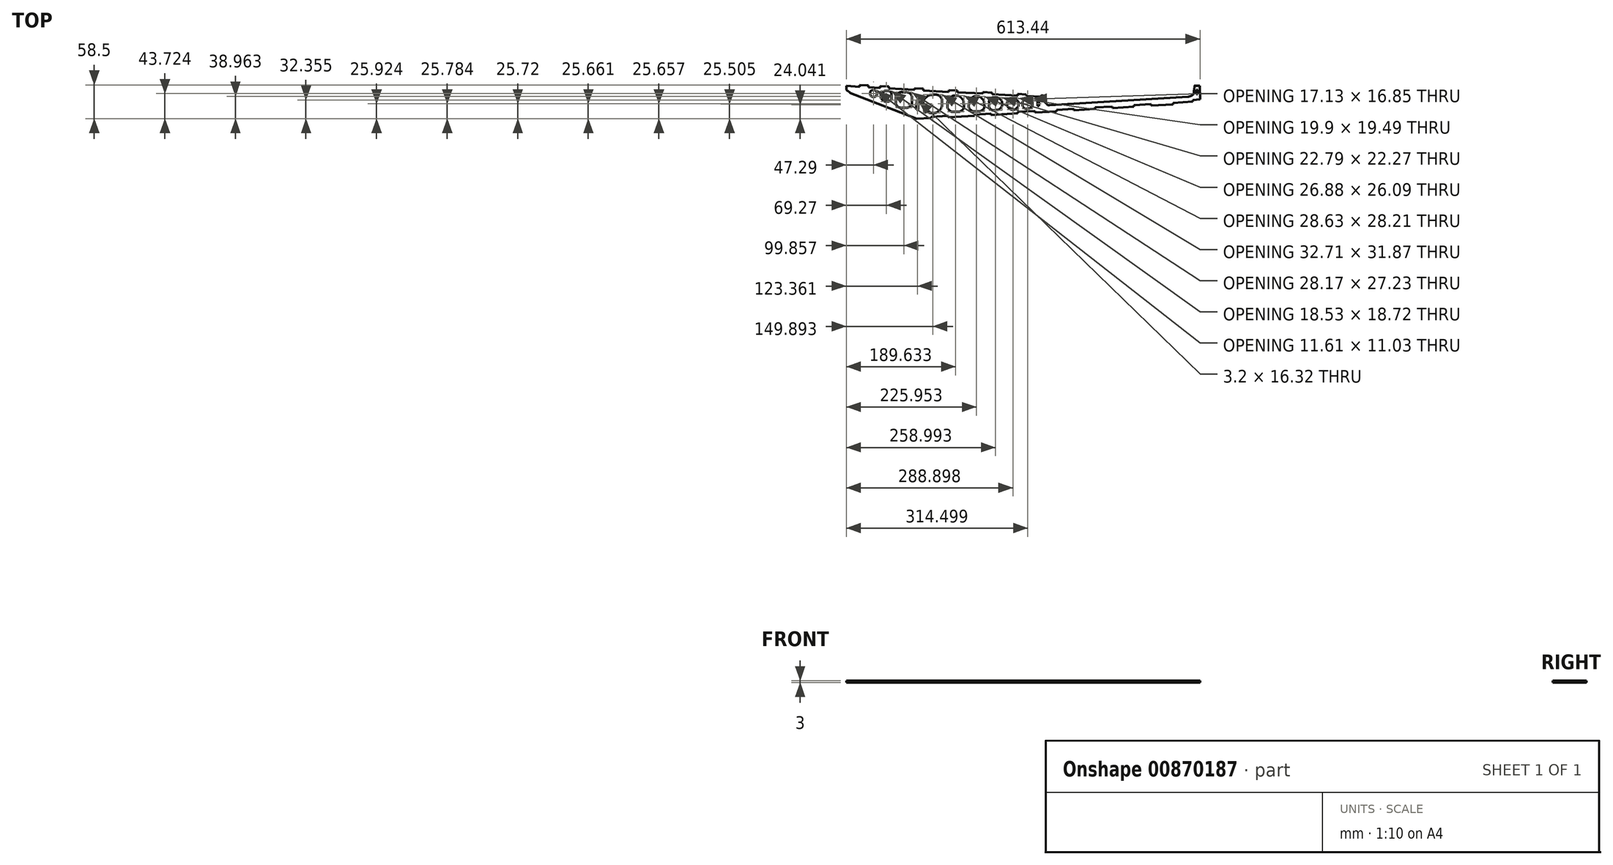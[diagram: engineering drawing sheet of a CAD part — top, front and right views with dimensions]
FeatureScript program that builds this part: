
annotation { "Feature Type Name" : "Feature", "Feature Type Description" : "" }
export const myFeature = defineFeature(function(context is Context, id is Id, definition is map)
    precondition{}
    {
        {
            var Q0;
            Q0=qCreatedBy(makeId("Top.planeOp"),FACE);
            var sketch = newSketch(context, id + "F0", { "sketchPlane" : qUnion([Q0])});
            skLineSegment(sketch, "E0", {"start": v(-306.53, 27.6) * mm, "end": v(-283.7, 26.24) * mm});
            skLineSegment(sketch, "E1", {"start": v(-283.7, 26.24) * mm, "end": v(-283.65, 29.25) * mm});
            skLineSegment(sketch, "E2", {"start": v(-283.65, 29.25) * mm, "end": v(-268.49, 28.33) * mm});
            skLineSegment(sketch, "E3", {"start": v(-268.49, 28.33) * mm, "end": v(-268.62, 25.37) * mm});
            skLineSegment(sketch, "E4", {"start": v(-268.62, 25.37) * mm, "end": v(-248.2, 24.14) * mm});
            skLineSegment(sketch, "E5", {"start": v(-248.2, 24.14) * mm, "end": v(-248.23, 27.11) * mm});
            skLineSegment(sketch, "E6", {"start": v(-248.23, 27.11) * mm, "end": v(-233.12, 26.42) * mm});
            skLineSegment(sketch, "E7", {"start": v(-233.12, 26.42) * mm, "end": v(-233.28, 23.32) * mm});
            skLineSegment(sketch, "E8", {"start": v(-233.28, 23.32) * mm, "end": v(-188.42, 20.66) * mm});
            skLineSegment(sketch, "E9", {"start": v(-188.42, 20.66) * mm, "end": v(-188.4, 23.56) * mm});
            skLineSegment(sketch, "E10", {"start": v(-188.4, 23.56) * mm, "end": v(-173.4, 22.68) * mm});
            skLineSegment(sketch, "E11", {"start": v(-173.4, 22.68) * mm, "end": v(-173.39, 19.88) * mm});
            skLineSegment(sketch, "E12", {"start": v(-173.39, 19.88) * mm, "end": v(-129.24, 17.14) * mm});
            skLineSegment(sketch, "E13", {"start": v(-129.24, 17.14) * mm, "end": v(-129.1, 20.23) * mm});
            skLineSegment(sketch, "E14", {"start": v(-129.1, 20.23) * mm, "end": v(-114.05, 19.46) * mm});
            skLineSegment(sketch, "E15", {"start": v(-114.05, 19.46) * mm, "end": v(-114.17, 16.65) * mm});
            skLineSegment(sketch, "E16", {"start": v(-114.17, 16.65) * mm, "end": v(-69.6, 14.2) * mm});
            skLineSegment(sketch, "E17", {"start": v(-69.6, 14.2) * mm, "end": v(-69.49, 16.95) * mm});
            skLineSegment(sketch, "E18", {"start": v(-69.49, 16.95) * mm, "end": v(-54.08, 15.88) * mm});
            skLineSegment(sketch, "E19", {"start": v(-54.08, 15.88) * mm, "end": v(-53.85, 13.26) * mm});
            skLineSegment(sketch, "E20", {"start": v(-53.85, 13.26) * mm, "end": v(-9.62, 10.9) * mm});
            skLineSegment(sketch, "E21", {"start": v(-9.62, 10.9) * mm, "end": v(-9.38, 14.01) * mm});
            skLineSegment(sketch, "E22", {"start": v(-9.38, 14.01) * mm, "end": v(5.44, 12.76) * mm});
            skLineSegment(sketch, "E23", {"start": v(5.44, 12.76) * mm, "end": v(5.67, 9.87) * mm});
            skLineSegment(sketch, "E24", {"start": v(5.67, 9.87) * mm, "end": v(31.56, 8.9) * mm});
            skLineSegment(sketch, "E25", {"start": v(31.56, 8.9) * mm, "end": v(31.93, 11.73) * mm});
            skLineSegment(sketch, "E26", {"start": v(45.61, -5.69) * mm, "end": v(285.73, 8.77) * mm});
            skLineSegment(sketch, "E27", {"start": v(296.22, 19.12) * mm, "end": v(297, 26.85) * mm});
            skLineSegment(sketch, "E28", {"start": v(298.34, 28) * mm, "end": v(306.34, 28.12) * mm});
            skLineSegment(sketch, "E29", {"start": v(306.34, 28.12) * mm, "end": v(306.53, 4.6) * mm});
            skLineSegment(sketch, "E30", {"start": v(306.53, 4.6) * mm, "end": v(294.22, 3.28) * mm});
            skLineSegment(sketch, "E31", {"start": v(294.22, 3.28) * mm, "end": v(294.32, 0.27) * mm});
            skLineSegment(sketch, "E32", {"start": v(294.32, 0.27) * mm, "end": v(259.45, -1.91) * mm});
            skLineSegment(sketch, "E33", {"start": v(259.45, -1.91) * mm, "end": v(259.47, -4.56) * mm});
            skLineSegment(sketch, "E34", {"start": v(259.47, -4.56) * mm, "end": v(221.44, -6.56) * mm});
            skLineSegment(sketch, "E35", {"start": v(221.44, -6.56) * mm, "end": v(221.44, -4.07) * mm});
            skLineSegment(sketch, "E36", {"start": v(221.44, -4.07) * mm, "end": v(191.93, -5.9) * mm});
            skLineSegment(sketch, "E37", {"start": v(191.93, -5.9) * mm, "end": v(191.94, -8.45) * mm});
            skLineSegment(sketch, "E38", {"start": v(191.94, -8.45) * mm, "end": v(154.85, -10.63) * mm});
            skLineSegment(sketch, "E39", {"start": v(154.85, -10.63) * mm, "end": v(154.7, -8.08) * mm});
            skLineSegment(sketch, "E40", {"start": v(154.7, -8.08) * mm, "end": v(124.72, -9.9) * mm});
            skLineSegment(sketch, "E41", {"start": v(124.72, -9.9) * mm, "end": v(124.67, -12.42) * mm});
            skLineSegment(sketch, "E42", {"start": v(124.67, -12.42) * mm, "end": v(87.6, -14.59) * mm});
            skLineSegment(sketch, "E43", {"start": v(87.6, -14.59) * mm, "end": v(87.58, -12.1) * mm});
            skLineSegment(sketch, "E44", {"start": v(87.58, -12.1) * mm, "end": v(57.75, -13.84) * mm});
            skLineSegment(sketch, "E45", {"start": v(57.75, -13.84) * mm, "end": v(57.8, -16.46) * mm});
            skLineSegment(sketch, "E46", {"start": v(57.8, -16.46) * mm, "end": v(20.34, -18.58) * mm});
            skLineSegment(sketch, "E47", {"start": v(20.34, -18.58) * mm, "end": v(20.34, -15.91) * mm});
            skLineSegment(sketch, "E48", {"start": v(20.34, -15.91) * mm, "end": v(-9.27, -17.5) * mm});
            skLineSegment(sketch, "E49", {"start": v(-9.27, -17.5) * mm, "end": v(-9.18, -20.1) * mm});
            skLineSegment(sketch, "E50", {"start": v(-9.18, -20.1) * mm, "end": v(-55.55, -22.72) * mm});
            skLineSegment(sketch, "E51", {"start": v(-55.55, -22.72) * mm, "end": v(-55.55, -20.4) * mm});
            skLineSegment(sketch, "E52", {"start": v(-55.55, -20.4) * mm, "end": v(-84.77, -22.06) * mm});
            skLineSegment(sketch, "E53", {"start": v(-84.77, -22.06) * mm, "end": v(-84.69, -24.35) * mm});
            skLineSegment(sketch, "E54", {"start": v(-84.69, -24.35) * mm, "end": v(-129.84, -26.56) * mm});
            skLineSegment(sketch, "E55", {"start": v(-129.84, -26.56) * mm, "end": v(-130.06, -24.37) * mm});
            skLineSegment(sketch, "E56", {"start": v(-130.06, -24.37) * mm, "end": v(-159.83, -26.09) * mm});
            skLineSegment(sketch, "E57", {"start": v(-159.83, -26.09) * mm, "end": v(-159.73, -28.23) * mm});
            skLineSegment(sketch, "E58", {"start": v(-159.73, -28.23) * mm, "end": v(-184.52, -29.25) * mm});
            skLineSegment(sketch, "E59", {"start": v(-184.52, -29.25) * mm, "end": v(-299.74, 15.36) * mm});
            skLineSegment(sketch, "E60", {"start": v(-306.53, 27.6) * mm, "end": v(-306.53, 27.6) * mm});
            skLineSegment(sketch, "E61", {"start": v(-184.99, 2.95) * mm, "end": v(-181.95, 2.95) * mm});
            skLineSegment(sketch, "E62", {"start": v(-181.95, 2.95) * mm, "end": v(-181.95, -13.37) * mm});
            skLineSegment(sketch, "E63", {"start": v(-181.95, -13.37) * mm, "end": v(-185.15, -13.21) * mm});
            skLineSegment(sketch, "E64", {"start": v(-185.15, -13.21) * mm, "end": v(-184.99, 2.95) * mm});
            skLineSegment(sketch, "E65", {"start": v(24.7, 0.17) * mm, "end": v(27.62, 0.08) * mm});
            skLineSegment(sketch, "E66", {"start": v(27.62, 0.08) * mm, "end": v(27.7, -7.13) * mm});
            skLineSegment(sketch, "E67", {"start": v(27.7, -7.13) * mm, "end": v(24.58, -7.19) * mm});
            skLineSegment(sketch, "E68", {"start": v(24.58, -7.19) * mm, "end": v(24.7, 0.17) * mm});
            skLineSegment(sketch, "E69", {"start": v(300.22, 21.04) * mm, "end": v(302.3, 21) * mm});
            skLineSegment(sketch, "E70", {"start": v(302.3, 21) * mm, "end": v(302.3, 13.07) * mm});
            skLineSegment(sketch, "E71", {"start": v(302.3, 13.07) * mm, "end": v(300.22, 13.03) * mm});
            skLineSegment(sketch, "E72", {"start": v(300.22, 13.03) * mm, "end": v(300.22, 21.04) * mm});
            skFitSpline(sketch, "E73", {"points": [v(31.93, 11.73) * mm, v(33.15, 10.85) * mm, v(34.88, 10.5) * mm, v(34.7, 8.21) * mm]});
            skFitSpline(sketch, "E74", {"points": [v(34.7, 8.21) * mm, v(35.27, 4.95) * mm, v(35.68, 1.68) * mm, v(38.01, -1.58) * mm]});
            skFitSpline(sketch, "E75", {"points": [v(38.01, -1.58) * mm, v(40.4, -3.36) * mm, v(42.65, -5.61) * mm, v(45.61, -5.69) * mm]});
            skFitSpline(sketch, "E76", {"points": [v(285.73, 8.77) * mm, v(290.42, 10.12) * mm, v(295.05, 13.44) * mm, v(296.22, 19.12) * mm]});
            skFitSpline(sketch, "E77", {"points": [v(297, 26.85) * mm, v(297, 26.85) * mm, v(297, 26.85) * mm, v(297.02, 26.92) * mm, v(297.6, 28.14) * mm, v(298.34, 28) * mm]});
            skFitSpline(sketch, "E78", {"points": [v(-299.74, 15.36) * mm, v(-303.25, 18.2) * mm, v(-306.38, 20.6) * mm, v(-306.53, 27.6) * mm]});
            skFitSpline(sketch, "E79", {"points": [v(-254, 14.47) * mm, v(-254, 11.52) * mm, v(-256.51, 9.13) * mm, v(-259.62, 9.13) * mm]});
            skFitSpline(sketch, "E80", {"points": [v(-259.62, 9.13) * mm, v(-262.73, 9.13) * mm, v(-265.24, 11.52) * mm, v(-265.24, 14.47) * mm]});
            skFitSpline(sketch, "E81", {"points": [v(-265.24, 14.47) * mm, v(-265.24, 17.42) * mm, v(-262.73, 19.81) * mm, v(-259.62, 19.81) * mm]});
            skFitSpline(sketch, "E82", {"points": [v(-259.62, 19.81) * mm, v(-256.51, 19.81) * mm, v(-254, 17.42) * mm, v(-254, 14.47) * mm]});
            skFitSpline(sketch, "E83", {"points": [v(-228.67, 9.71) * mm, v(-228.67, 4.7) * mm, v(-232.74, 0.65) * mm, v(-237.76, 0.65) * mm]});
            skFitSpline(sketch, "E84", {"points": [v(-237.76, 0.65) * mm, v(-240.16, 0.65) * mm, v(-242.48, 1.6) * mm, v(-244.18, 3.3) * mm]});
            skFitSpline(sketch, "E85", {"points": [v(-244.18, 3.3) * mm, v(-245.88, 5) * mm, v(-246.84, 7.3) * mm, v(-246.84, 9.71) * mm]});
            skFitSpline(sketch, "E86", {"points": [v(-246.84, 9.71) * mm, v(-246.84, 12.12) * mm, v(-245.88, 14.42) * mm, v(-244.18, 16.12) * mm]});
            skFitSpline(sketch, "E87", {"points": [v(-244.18, 16.12) * mm, v(-242.48, 17.82) * mm, v(-240.16, 18.78) * mm, v(-237.76, 18.78) * mm]});
            skFitSpline(sketch, "E88", {"points": [v(-237.76, 18.78) * mm, v(-232.74, 18.78) * mm, v(-228.67, 14.72) * mm, v(-228.67, 9.71) * mm]});
            skFitSpline(sketch, "E89", {"points": [v(-193.4, 3.1) * mm, v(-193.4, -4.18) * mm, v(-199.52, -10.08) * mm, v(-207.05, -10.08) * mm]});
            skFitSpline(sketch, "E90", {"points": [v(-207.05, -10.08) * mm, v(-214.59, -10.08) * mm, v(-220.7, -4.18) * mm, v(-220.7, 3.1) * mm]});
            skFitSpline(sketch, "E91", {"points": [v(-220.7, 3.1) * mm, v(-220.7, 10.39) * mm, v(-214.59, 16.29) * mm, v(-207.05, 16.29) * mm]});
            skFitSpline(sketch, "E92", {"points": [v(-207.05, 16.29) * mm, v(-199.52, 16.29) * mm, v(-193.4, 10.39) * mm, v(-193.4, 3.1) * mm]});
            skFitSpline(sketch, "E93", {"points": [v(-141.18, -3.73) * mm, v(-141.18, -7.87) * mm, v(-142.87, -11.85) * mm, v(-145.88, -14.78) * mm]});
            skFitSpline(sketch, "E94", {"points": [v(-145.88, -14.78) * mm, v(-148.89, -17.7) * mm, v(-152.97, -19.35) * mm, v(-157.22, -19.35) * mm]});
            skFitSpline(sketch, "E95", {"points": [v(-157.22, -19.35) * mm, v(-161.47, -19.35) * mm, v(-165.55, -17.7) * mm, v(-168.56, -14.78) * mm]});
            skFitSpline(sketch, "E96", {"points": [v(-168.56, -14.78) * mm, v(-171.57, -11.85) * mm, v(-173.26, -7.87) * mm, v(-173.26, -3.73) * mm]});
            skFitSpline(sketch, "E97", {"points": [v(-173.26, -3.73) * mm, v(-173.26, 0.42) * mm, v(-171.57, 4.39) * mm, v(-168.56, 7.32) * mm]});
            skFitSpline(sketch, "E98", {"points": [v(-168.56, 7.32) * mm, v(-165.55, 10.25) * mm, v(-161.47, 11.9) * mm, v(-157.22, 11.9) * mm]});
            skFitSpline(sketch, "E99", {"points": [v(-157.22, 11.9) * mm, v(-148.36, 11.9) * mm, v(-141.18, 4.9) * mm, v(-141.18, -3.73) * mm]});
            skFitSpline(sketch, "E100", {"points": [v(-103.41, -3.15) * mm, v(-103.41, -10.79) * mm, v(-109.62, -16.98) * mm, v(-117.28, -16.98) * mm]});
            skFitSpline(sketch, "E101", {"points": [v(-117.28, -16.98) * mm, v(-124.93, -16.98) * mm, v(-131.14, -10.79) * mm, v(-131.14, -3.15) * mm]});
            skFitSpline(sketch, "E102", {"points": [v(-131.14, -3.15) * mm, v(-131.14, 0.52) * mm, v(-129.68, 4.04) * mm, v(-127.08, 6.63) * mm]});
            skFitSpline(sketch, "E103", {"points": [v(-127.08, 6.63) * mm, v(-124.48, 9.22) * mm, v(-120.95, 10.68) * mm, v(-117.28, 10.68) * mm]});
            skFitSpline(sketch, "E104", {"points": [v(-117.28, 10.68) * mm, v(-113.6, 10.68) * mm, v(-110.07, 9.22) * mm, v(-107.47, 6.63) * mm]});
            skFitSpline(sketch, "E105", {"points": [v(-107.47, 6.63) * mm, v(-104.87, 4.04) * mm, v(-103.41, 0.52) * mm, v(-103.41, -3.15) * mm]});
            skFitSpline(sketch, "E106", {"points": [v(-67.94, -3.43) * mm, v(-67.94, -10.5) * mm, v(-73.77, -16.22) * mm, v(-80.96, -16.22) * mm]});
            skFitSpline(sketch, "E107", {"points": [v(-80.96, -16.22) * mm, v(-88.15, -16.22) * mm, v(-93.97, -10.5) * mm, v(-93.97, -3.43) * mm]});
            skFitSpline(sketch, "E108", {"points": [v(-93.97, -3.43) * mm, v(-93.97, -0.03) * mm, v(-92.6, 3.22) * mm, v(-90.16, 5.62) * mm]});
            skFitSpline(sketch, "E109", {"points": [v(-90.16, 5.62) * mm, v(-87.72, 8.02) * mm, v(-84.4, 9.37) * mm, v(-80.96, 9.37) * mm]});
            skFitSpline(sketch, "E110", {"points": [v(-80.96, 9.37) * mm, v(-77.5, 9.37) * mm, v(-74.2, 8.02) * mm, v(-71.75, 5.62) * mm]});
            skFitSpline(sketch, "E111", {"points": [v(-71.75, 5.62) * mm, v(-69.31, 3.22) * mm, v(-67.94, -0.03) * mm, v(-67.94, -3.43) * mm]});
            skFitSpline(sketch, "E112", {"points": [v(-36.6, -3.47) * mm, v(-36.6, -6.33) * mm, v(-37.78, -9.07) * mm, v(-39.87, -11.1) * mm]});
            skFitSpline(sketch, "E113", {"points": [v(-39.87, -11.1) * mm, v(-41.97, -13.12) * mm, v(-44.81, -14.25) * mm, v(-47.78, -14.25) * mm]});
            skFitSpline(sketch, "E114", {"points": [v(-47.78, -14.25) * mm, v(-53.95, -14.25) * mm, v(-58.95, -9.42) * mm, v(-58.95, -3.47) * mm]});
            skFitSpline(sketch, "E115", {"points": [v(-58.95, -3.47) * mm, v(-58.95, 2.5) * mm, v(-53.95, 7.32) * mm, v(-47.78, 7.32) * mm]});
            skFitSpline(sketch, "E116", {"points": [v(-47.78, 7.32) * mm, v(-44.81, 7.32) * mm, v(-41.97, 6.18) * mm, v(-39.87, 4.16) * mm]});
            skFitSpline(sketch, "E117", {"points": [v(-39.87, 4.16) * mm, v(-37.78, 2.14) * mm, v(-36.6, -0.6) * mm, v(-36.6, -3.47) * mm]});
            skFitSpline(sketch, "E118", {"points": [v(-8.13, -3.75) * mm, v(-8.13, -6.31) * mm, v(-9.17, -8.77) * mm, v(-11.02, -10.59) * mm]});
            skFitSpline(sketch, "E119", {"points": [v(-11.02, -10.59) * mm, v(-12.88, -12.4) * mm, v(-15.4, -13.42) * mm, v(-18.01, -13.42) * mm]});
            skFitSpline(sketch, "E120", {"points": [v(-18.01, -13.42) * mm, v(-20.63, -13.42) * mm, v(-23.15, -12.4) * mm, v(-25, -10.59) * mm]});
            skFitSpline(sketch, "E121", {"points": [v(-25, -10.59) * mm, v(-26.85, -8.77) * mm, v(-27.9, -6.31) * mm, v(-27.9, -3.75) * mm]});
            skFitSpline(sketch, "E122", {"points": [v(-27.9, -3.75) * mm, v(-27.9, -1.18) * mm, v(-26.85, 1.28) * mm, v(-25, 3.1) * mm]});
            skFitSpline(sketch, "E123", {"points": [v(-25, 3.1) * mm, v(-23.15, 4.91) * mm, v(-20.63, 5.93) * mm, v(-18.01, 5.93) * mm]});
            skFitSpline(sketch, "E124", {"points": [v(-18.01, 5.93) * mm, v(-15.4, 5.93) * mm, v(-12.88, 4.91) * mm, v(-11.02, 3.1) * mm]});
            skFitSpline(sketch, "E125", {"points": [v(-11.02, 3.1) * mm, v(-9.17, 1.28) * mm, v(-8.13, -1.18) * mm, v(-8.13, -3.75) * mm]});
            skFitSpline(sketch, "E126", {"points": [v(16.1, -3.6) * mm, v(16.1, -5.76) * mm, v(15.2, -7.83) * mm, v(13.63, -9.36) * mm]});
            skFitSpline(sketch, "E127", {"points": [v(13.63, -9.36) * mm, v(12.06, -10.9) * mm, v(9.92, -11.75) * mm, v(7.7, -11.75) * mm]});
            skFitSpline(sketch, "E128", {"points": [v(7.7, -11.75) * mm, v(3.06, -11.75) * mm, v(-0.7, -8.1) * mm, v(-0.7, -3.6) * mm]});
            skFitSpline(sketch, "E129", {"points": [v(-0.7, -3.6) * mm, v(-0.7, 0.91) * mm, v(3.06, 4.57) * mm, v(7.7, 4.57) * mm]});
            skFitSpline(sketch, "E130", {"points": [v(7.7, 4.57) * mm, v(9.92, 4.57) * mm, v(12.06, 3.7) * mm, v(13.63, 2.18) * mm]});
            skFitSpline(sketch, "E131", {"points": [v(13.63, 2.18) * mm, v(15.2, 0.65) * mm, v(16.1, -1.43) * mm, v(16.1, -3.6) * mm]});
            skSolve(sketch);
        }
        {
            var Q0;
            Q0 = qSketchRegion(id + "F0", true);
            extrude(context, id + "F1", {"entities" : qUnion([Q0]), "depth" : 3 * mm, "offsetDistance" : 25 * mm});
        }
    });
